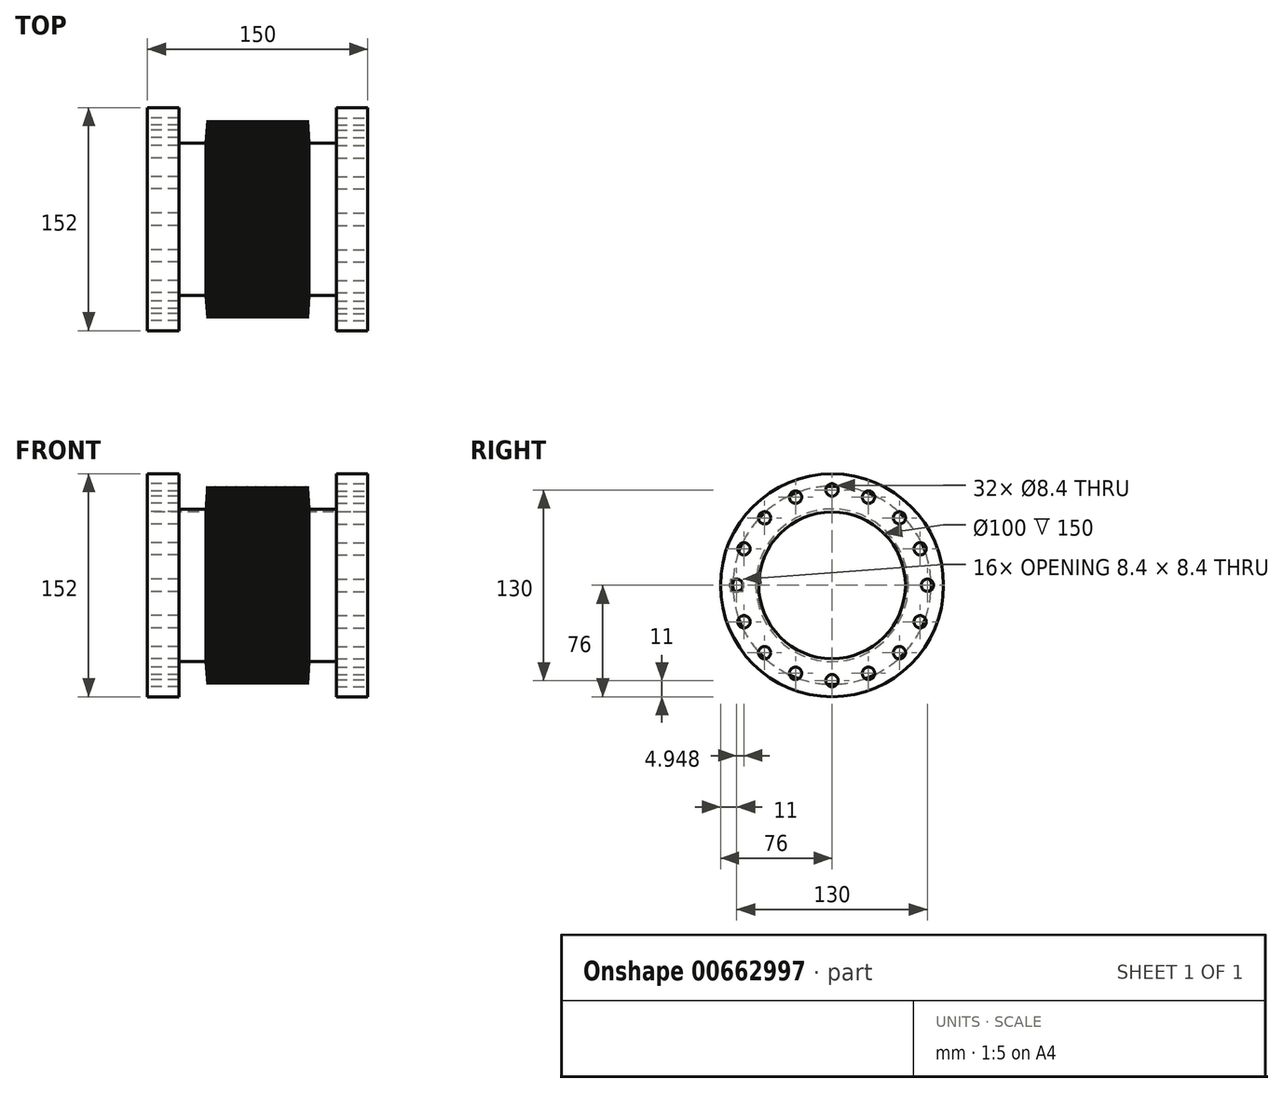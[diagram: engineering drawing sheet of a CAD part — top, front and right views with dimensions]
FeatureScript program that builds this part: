
annotation { "Feature Type Name" : "Feature", "Feature Type Description" : "" }
export const myFeature = defineFeature(function(context is Context, id is Id, definition is map)
    precondition{}
    {
        {
            var Q0;
            Q0=qCreatedBy(makeId("Front.planeOp"),FACE);
            var sketch = newSketch(context, id + "F0", { "sketchPlane" : qUnion([Q0])});
            skLineSegment(sketch, "E0", {"start": v(0, 50) * mm, "end": v(0, 76) * mm});
            skLineSegment(sketch, "E1", {"start": v(0, 76) * mm, "end": v(21.3, 76) * mm});
            skLineSegment(sketch, "E2", {"start": v(21.3, 76) * mm, "end": v(21.3, 52) * mm});
            skLineSegment(sketch, "E3", {"start": v(21.3, 52) * mm, "end": v(40, 52) * mm});
            skLineSegment(sketch, "E4", {"start": v(40, 52) * mm, "end": v(41, 67.5) * mm});
            skLineSegment(sketch, "E5", {"start": v(41, 67.5) * mm, "end": v(42, 52) * mm});
            skLineSegment(sketch, "E6", {"start": v(41, 67.5) * mm, "end": v(41, 52) * mm, "construction": true});
            skLineSegment(sketch, "E7", {"start": v(40, 52) * mm, "end": v(41, 52) * mm, "construction": true});
            skLineSegment(sketch, "E8", {"start": v(41, 52) * mm, "end": v(42, 52) * mm, "construction": true});
            skLineSegment(sketch, "E9.1.0.0", {"start": v(42, 52) * mm, "end": v(43, 67.5) * mm});
            skLineSegment(sketch, "E9.1.0.1", {"start": v(43, 67.5) * mm, "end": v(44, 52) * mm});
            skLineSegment(sketch, "E9.2.0.0", {"start": v(44, 52) * mm, "end": v(45, 67.5) * mm});
            skLineSegment(sketch, "E9.2.0.1", {"start": v(45, 67.5) * mm, "end": v(46, 52) * mm});
            skLineSegment(sketch, "E9.3.0.0", {"start": v(46, 52) * mm, "end": v(47, 67.5) * mm});
            skLineSegment(sketch, "E9.3.0.1", {"start": v(47, 67.5) * mm, "end": v(48, 52) * mm});
            skLineSegment(sketch, "E9.4.0.0", {"start": v(48, 52) * mm, "end": v(49, 67.5) * mm});
            skLineSegment(sketch, "E9.4.0.1", {"start": v(49, 67.5) * mm, "end": v(50, 52) * mm});
            skLineSegment(sketch, "E9.5.0.0", {"start": v(50, 52) * mm, "end": v(51, 67.5) * mm});
            skLineSegment(sketch, "E9.5.0.1", {"start": v(51, 67.5) * mm, "end": v(52, 52) * mm});
            skLineSegment(sketch, "E9.6.0.0", {"start": v(52, 52) * mm, "end": v(53, 67.5) * mm});
            skLineSegment(sketch, "E9.6.0.1", {"start": v(53, 67.5) * mm, "end": v(54, 52) * mm});
            skLineSegment(sketch, "E9.7.0.0", {"start": v(54, 52) * mm, "end": v(55, 67.5) * mm});
            skLineSegment(sketch, "E9.7.0.1", {"start": v(55, 67.5) * mm, "end": v(56, 52) * mm});
            skLineSegment(sketch, "E9.8.0.0", {"start": v(56, 52) * mm, "end": v(57, 67.5) * mm});
            skLineSegment(sketch, "E9.8.0.1", {"start": v(57, 67.5) * mm, "end": v(58, 52) * mm});
            skLineSegment(sketch, "E9.9.0.0", {"start": v(58, 52) * mm, "end": v(59, 67.5) * mm});
            skLineSegment(sketch, "E9.9.0.1", {"start": v(59, 67.5) * mm, "end": v(60, 52) * mm});
            skLineSegment(sketch, "E9.10.0.0", {"start": v(60, 52) * mm, "end": v(61, 67.5) * mm});
            skLineSegment(sketch, "E9.10.0.1", {"start": v(61, 67.5) * mm, "end": v(62, 52) * mm});
            skLineSegment(sketch, "E9.11.0.0", {"start": v(62, 52) * mm, "end": v(63, 67.5) * mm});
            skLineSegment(sketch, "E9.11.0.1", {"start": v(63, 67.5) * mm, "end": v(64, 52) * mm});
            skLineSegment(sketch, "E9.12.0.0", {"start": v(64, 52) * mm, "end": v(65, 67.5) * mm});
            skLineSegment(sketch, "E9.12.0.1", {"start": v(65, 67.5) * mm, "end": v(66, 52) * mm});
            skLineSegment(sketch, "E9.13.0.0", {"start": v(66, 52) * mm, "end": v(67, 67.5) * mm});
            skLineSegment(sketch, "E9.13.0.1", {"start": v(67, 67.5) * mm, "end": v(68, 52) * mm});
            skLineSegment(sketch, "E9.14.0.0", {"start": v(68, 52) * mm, "end": v(69, 67.5) * mm});
            skLineSegment(sketch, "E9.14.0.1", {"start": v(69, 67.5) * mm, "end": v(70, 52) * mm});
            skLineSegment(sketch, "E9.15.0.0", {"start": v(70, 52) * mm, "end": v(71, 67.5) * mm});
            skLineSegment(sketch, "E9.15.0.1", {"start": v(71, 67.5) * mm, "end": v(72, 52) * mm});
            skLineSegment(sketch, "E9.16.0.0", {"start": v(72, 52) * mm, "end": v(73, 67.5) * mm});
            skLineSegment(sketch, "E9.16.0.1", {"start": v(73, 67.5) * mm, "end": v(74, 52) * mm});
            skLineSegment(sketch, "E9.17.0.0", {"start": v(74, 52) * mm, "end": v(75, 67.5) * mm});
            skLineSegment(sketch, "E9.17.0.1", {"start": v(75, 67.5) * mm, "end": v(76, 52) * mm});
            skLineSegment(sketch, "E9.18.0.0", {"start": v(76, 52) * mm, "end": v(77, 67.5) * mm});
            skLineSegment(sketch, "E9.18.0.1", {"start": v(77, 67.5) * mm, "end": v(78, 52) * mm});
            skLineSegment(sketch, "E9.19.0.0", {"start": v(78, 52) * mm, "end": v(79, 67.5) * mm});
            skLineSegment(sketch, "E9.19.0.1", {"start": v(79, 67.5) * mm, "end": v(80, 52) * mm});
            skLineSegment(sketch, "E9.20.0.0", {"start": v(80, 52) * mm, "end": v(81, 67.5) * mm});
            skLineSegment(sketch, "E9.20.0.1", {"start": v(81, 67.5) * mm, "end": v(82, 52) * mm});
            skLineSegment(sketch, "E9.21.0.0", {"start": v(82, 52) * mm, "end": v(83, 67.5) * mm});
            skLineSegment(sketch, "E9.21.0.1", {"start": v(83, 67.5) * mm, "end": v(84, 52) * mm});
            skLineSegment(sketch, "E9.22.0.0", {"start": v(84, 52) * mm, "end": v(85, 67.5) * mm});
            skLineSegment(sketch, "E9.22.0.1", {"start": v(85, 67.5) * mm, "end": v(86, 52) * mm});
            skLineSegment(sketch, "E9.23.0.0", {"start": v(86, 52) * mm, "end": v(87, 67.5) * mm});
            skLineSegment(sketch, "E9.23.0.1", {"start": v(87, 67.5) * mm, "end": v(88, 52) * mm});
            skLineSegment(sketch, "E9.24.0.0", {"start": v(88, 52) * mm, "end": v(89, 67.5) * mm});
            skLineSegment(sketch, "E9.24.0.1", {"start": v(89, 67.5) * mm, "end": v(90, 52) * mm});
            skLineSegment(sketch, "E9.25.0.0", {"start": v(90, 52) * mm, "end": v(91, 67.5) * mm});
            skLineSegment(sketch, "E9.25.0.1", {"start": v(91, 67.5) * mm, "end": v(92, 52) * mm});
            skLineSegment(sketch, "E9.26.0.0", {"start": v(92, 52) * mm, "end": v(93, 67.5) * mm});
            skLineSegment(sketch, "E9.26.0.1", {"start": v(93, 67.5) * mm, "end": v(94, 52) * mm});
            skLineSegment(sketch, "E9.27.0.0", {"start": v(94, 52) * mm, "end": v(95, 67.5) * mm});
            skLineSegment(sketch, "E9.27.0.1", {"start": v(95, 67.5) * mm, "end": v(96, 52) * mm});
            skLineSegment(sketch, "E9.28.0.0", {"start": v(96, 52) * mm, "end": v(97, 67.5) * mm});
            skLineSegment(sketch, "E9.28.0.1", {"start": v(97, 67.5) * mm, "end": v(98, 52) * mm});
            skLineSegment(sketch, "E9.29.0.0", {"start": v(98, 52) * mm, "end": v(99, 67.5) * mm});
            skLineSegment(sketch, "E9.29.0.1", {"start": v(99, 67.5) * mm, "end": v(100, 52) * mm});
            skLineSegment(sketch, "E9.30.0.0", {"start": v(100, 52) * mm, "end": v(101, 67.5) * mm});
            skLineSegment(sketch, "E9.30.0.1", {"start": v(101, 67.5) * mm, "end": v(102, 52) * mm});
            skLineSegment(sketch, "E9.31.0.0", {"start": v(102, 52) * mm, "end": v(103, 67.5) * mm});
            skLineSegment(sketch, "E9.31.0.1", {"start": v(103, 67.5) * mm, "end": v(104, 52) * mm});
            skLineSegment(sketch, "E9.32.0.0", {"start": v(104, 52) * mm, "end": v(105, 67.5) * mm});
            skLineSegment(sketch, "E9.32.0.1", {"start": v(105, 67.5) * mm, "end": v(106, 52) * mm});
            skLineSegment(sketch, "E9.33.0.0", {"start": v(106, 52) * mm, "end": v(107, 67.5) * mm});
            skLineSegment(sketch, "E9.33.0.1", {"start": v(107, 67.5) * mm, "end": v(108, 52) * mm});
            skLineSegment(sketch, "E9.34.0.0", {"start": v(108, 52) * mm, "end": v(109, 67.5) * mm});
            skLineSegment(sketch, "E9.34.0.1", {"start": v(109, 67.5) * mm, "end": v(110, 52) * mm});
            skLineSegment(sketch, "E9.direction1", {"start": v(40, 52) * mm, "end": v(42, 52) * mm, "construction": true});
            skLineSegment(sketch, "E10", {"start": v(110, 52) * mm, "end": v(128.7, 52) * mm});
            skLineSegment(sketch, "E11", {"start": v(128.7, 52) * mm, "end": v(128.7, 76) * mm});
            skLineSegment(sketch, "E12", {"start": v(128.7, 76) * mm, "end": v(150, 76) * mm});
            skLineSegment(sketch, "E13", {"start": v(150, 76) * mm, "end": v(150, 50) * mm});
            skLineSegment(sketch, "E14", {"start": v(150, 50) * mm, "end": v(0, 50) * mm});
            skSolve(sketch);
        }
        {
            var Q0;
            Q0=qCreatedBy(makeId("Front.planeOp"),FACE);
            var sketch = newSketch(context, id + "F1", { "sketchPlane" : qUnion([Q0])});
            skLineSegment(sketch, "E15", {"start": v(0, 0) * mm, "end": v(75.04, 0) * mm});
            skSolve(sketch);
        }
        {
            var Q0;
            Q0=makeQuery(id+"F0.imprint","IMPRINT",FACE,{"disambiguationData":[TD([[makeQuery(id+"F0.imprint","IMPRINT",EDGE,{"derivedFrom":sQuery(id+"F0.wireOp",EDGE,"E0")}),-1.0]])]});
            var Q1;
            Q1=sQuery(id+"F1.wireOp",EDGE,"E15");
            revolve(context, id + "F2", {"surfaceOperationType" : NewSurfaceOperationType.NEW, "entities" : qUnion([Q0]), "axis" : qUnion([Q1]), "revolveType" : RevolveType.FULL});
        }
        {
            var Q0;
            Q0=makeQuery(id+"F2.opRevolve","SWEPT_FACE",FACE,{"disambiguationData":[OSD([sQuery(id+"F0.wireOp",EDGE,"E0")])]});
            var sketch = newSketch(context, id + "F3", { "sketchPlane" : qUnion([Q0])});
            skCircle(sketch, "E16", {"center": v(0, 0) * mm, "radius": 65 * mm, "construction": true});
            skPoint(sketch, "E17", {"position": v(-65, 0) * mm});
            skLineSegment(sketch, "E18", {"start": v(-65, 0) * mm, "end": v(0, 0) * mm, "construction": true});
            skPoint(sketch, "E19.1.0", {"position": v(-60.05, -24.87) * mm});
            skPoint(sketch, "E19.2.0", {"position": v(-45.96, -45.96) * mm});
            skPoint(sketch, "E19.3.0", {"position": v(-24.87, -60.05) * mm});
            skPoint(sketch, "E19.4.0", {"position": v(0, -65) * mm});
            skPoint(sketch, "E19.5.0", {"position": v(24.87, -60.05) * mm});
            skPoint(sketch, "E19.6.0", {"position": v(45.96, -45.96) * mm});
            skPoint(sketch, "E19.7.0", {"position": v(60.05, -24.87) * mm});
            skPoint(sketch, "E20.0.8.0", {"position": v(65, 0) * mm});
            skPoint(sketch, "E20.0.9.0", {"position": v(60.05, 24.87) * mm});
            skPoint(sketch, "E20.0.10.0", {"position": v(45.96, 45.96) * mm});
            skPoint(sketch, "E20.0.11.0", {"position": v(24.87, 60.05) * mm});
            skPoint(sketch, "E20.0.12.0", {"position": v(0, 65) * mm});
            skPoint(sketch, "E20.0.13.0", {"position": v(-24.87, 60.05) * mm});
            skPoint(sketch, "E20.0.14.0", {"position": v(-45.96, 45.96) * mm});
            skPoint(sketch, "E20.0.15.0", {"position": v(-60.05, 24.87) * mm});
            skSolve(sketch);
        }
        {
            var Q0;
            Q0=sQuery(id+"F3.wireOp",VERTEX,"E17");
            var Q1;
            Q1=sQuery(id+"F3.wireOp",VERTEX,"E19.7.0");
            var Q2;
            Q2=sQuery(id+"F3.wireOp",VERTEX,"E19.6.0");
            var Q3;
            Q3=sQuery(id+"F3.wireOp",VERTEX,"E19.5.0");
            var Q4;
            Q4=sQuery(id+"F3.wireOp",VERTEX,"E19.4.0");
            var Q5;
            Q5=sQuery(id+"F3.wireOp",VERTEX,"E19.3.0");
            var Q6;
            Q6=sQuery(id+"F3.wireOp",VERTEX,"E19.2.0");
            var Q7;
            Q7=sQuery(id+"F3.wireOp",VERTEX,"E19.1.0");
            var Q8;
            Q8=sQuery(id+"F3.wireOp",VERTEX,"E20.0.15.0");
            var Q9;
            Q9=sQuery(id+"F3.wireOp",VERTEX,"E20.0.14.0");
            var Q10;
            Q10=sQuery(id+"F3.wireOp",VERTEX,"E20.0.13.0");
            var Q11;
            Q11=sQuery(id+"F3.wireOp",VERTEX,"E20.0.12.0");
            var Q12;
            Q12=sQuery(id+"F3.wireOp",VERTEX,"E20.0.11.0");
            var Q13;
            Q13=sQuery(id+"F3.wireOp",VERTEX,"E20.0.10.0");
            var Q14;
            Q14=sQuery(id+"F3.wireOp",VERTEX,"E20.0.9.0");
            var Q15;
            Q15=sQuery(id+"F3.wireOp",VERTEX,"E20.0.8.0");
            var Q16;
            Q16=makeQuery(id+"F2.opRevolve","SWEPT_BODY",BODY,{"disambiguationData":[OSD([sQuery(id+"F0.wireOp",EDGE,"E0"),sQuery(id+"F0.wireOp",EDGE,"E1"),sQuery(id+"F0.wireOp",EDGE,"E2"),sQuery(id+"F0.wireOp",EDGE,"E3"),sQuery(id+"F0.wireOp",EDGE,"E4"),sQuery(id+"F0.wireOp",EDGE,"E5"),sQuery(id+"F0.wireOp",EDGE,"E9.1.0.0"),sQuery(id+"F0.wireOp",EDGE,"E9.1.0.1"),sQuery(id+"F0.wireOp",EDGE,"E9.2.0.0"),sQuery(id+"F0.wireOp",EDGE,"E9.2.0.1"),sQuery(id+"F0.wireOp",EDGE,"E9.3.0.0"),sQuery(id+"F0.wireOp",EDGE,"E9.3.0.1"),sQuery(id+"F0.wireOp",EDGE,"E9.4.0.0"),sQuery(id+"F0.wireOp",EDGE,"E9.4.0.1"),sQuery(id+"F0.wireOp",EDGE,"E9.5.0.0"),sQuery(id+"F0.wireOp",EDGE,"E9.5.0.1"),sQuery(id+"F0.wireOp",EDGE,"E9.6.0.0"),sQuery(id+"F0.wireOp",EDGE,"E9.6.0.1"),sQuery(id+"F0.wireOp",EDGE,"E9.7.0.0"),sQuery(id+"F0.wireOp",EDGE,"E9.7.0.1"),sQuery(id+"F0.wireOp",EDGE,"E9.8.0.0"),sQuery(id+"F0.wireOp",EDGE,"E9.8.0.1"),sQuery(id+"F0.wireOp",EDGE,"E9.9.0.0"),sQuery(id+"F0.wireOp",EDGE,"E9.9.0.1"),sQuery(id+"F0.wireOp",EDGE,"E9.10.0.0"),sQuery(id+"F0.wireOp",EDGE,"E9.10.0.1"),sQuery(id+"F0.wireOp",EDGE,"E9.11.0.0"),sQuery(id+"F0.wireOp",EDGE,"E9.11.0.1"),sQuery(id+"F0.wireOp",EDGE,"E9.12.0.0"),sQuery(id+"F0.wireOp",EDGE,"E9.12.0.1"),sQuery(id+"F0.wireOp",EDGE,"E9.13.0.0"),sQuery(id+"F0.wireOp",EDGE,"E9.13.0.1"),sQuery(id+"F0.wireOp",EDGE,"E9.14.0.0"),sQuery(id+"F0.wireOp",EDGE,"E9.14.0.1"),sQuery(id+"F0.wireOp",EDGE,"E9.15.0.0"),sQuery(id+"F0.wireOp",EDGE,"E9.15.0.1"),sQuery(id+"F0.wireOp",EDGE,"E9.16.0.0"),sQuery(id+"F0.wireOp",EDGE,"E9.16.0.1"),sQuery(id+"F0.wireOp",EDGE,"E9.17.0.0"),sQuery(id+"F0.wireOp",EDGE,"E9.17.0.1"),sQuery(id+"F0.wireOp",EDGE,"E9.18.0.0"),sQuery(id+"F0.wireOp",EDGE,"E9.18.0.1"),sQuery(id+"F0.wireOp",EDGE,"E9.19.0.0"),sQuery(id+"F0.wireOp",EDGE,"E9.19.0.1"),sQuery(id+"F0.wireOp",EDGE,"E9.20.0.0"),sQuery(id+"F0.wireOp",EDGE,"E9.20.0.1"),sQuery(id+"F0.wireOp",EDGE,"E9.21.0.0"),sQuery(id+"F0.wireOp",EDGE,"E9.21.0.1"),sQuery(id+"F0.wireOp",EDGE,"E9.22.0.0"),sQuery(id+"F0.wireOp",EDGE,"E9.22.0.1"),sQuery(id+"F0.wireOp",EDGE,"E9.23.0.0"),sQuery(id+"F0.wireOp",EDGE,"E9.23.0.1"),sQuery(id+"F0.wireOp",EDGE,"E9.24.0.0"),sQuery(id+"F0.wireOp",EDGE,"E9.24.0.1"),sQuery(id+"F0.wireOp",EDGE,"E9.25.0.0"),sQuery(id+"F0.wireOp",EDGE,"E9.25.0.1"),sQuery(id+"F0.wireOp",EDGE,"E9.26.0.0"),sQuery(id+"F0.wireOp",EDGE,"E9.26.0.1"),sQuery(id+"F0.wireOp",EDGE,"E9.27.0.0"),sQuery(id+"F0.wireOp",EDGE,"E9.27.0.1"),sQuery(id+"F0.wireOp",EDGE,"E9.28.0.0"),sQuery(id+"F0.wireOp",EDGE,"E9.28.0.1"),sQuery(id+"F0.wireOp",EDGE,"E9.29.0.0"),sQuery(id+"F0.wireOp",EDGE,"E9.29.0.1"),sQuery(id+"F0.wireOp",EDGE,"E9.30.0.0"),sQuery(id+"F0.wireOp",EDGE,"E9.30.0.1"),sQuery(id+"F0.wireOp",EDGE,"E9.31.0.0"),sQuery(id+"F0.wireOp",EDGE,"E9.31.0.1"),sQuery(id+"F0.wireOp",EDGE,"E9.32.0.0"),sQuery(id+"F0.wireOp",EDGE,"E9.32.0.1"),sQuery(id+"F0.wireOp",EDGE,"E9.33.0.0"),sQuery(id+"F0.wireOp",EDGE,"E9.33.0.1"),sQuery(id+"F0.wireOp",EDGE,"E9.34.0.0"),sQuery(id+"F0.wireOp",EDGE,"E9.34.0.1"),sQuery(id+"F0.wireOp",EDGE,"E10"),sQuery(id+"F0.wireOp",EDGE,"E11"),sQuery(id+"F0.wireOp",EDGE,"E12"),sQuery(id+"F0.wireOp",EDGE,"E13"),sQuery(id+"F0.wireOp",EDGE,"E14")])]});
            hole(context, id + "F4", {"style" : HoleStyle.SIMPLE, "endStyle" : HoleEndStyle.BLIND, "standardTappedOrClearance" : lookupTablePath({ "fit" : "Close", "standard" : "ISO", "size" : "M8", "type" : "Clearance" }), "standardBlindInLast" : lookupTablePath({ "fit" : "Close", "standard" : "ISO", "engagement" : "75%", "pitch" : "1.25 mm", "size" : "M8", "type" : "Clearance & tapped" }), "holeDiameter" : 8.4 * mm, "majorDiameter" : 5 * mm, "holeDepth" : 24 * mm, "isTappedThrough" : true, "tappedDepth" : 12 * mm, "tapClearance" : 3, "locations" : qUnion([Q0, Q1, Q2, Q3, Q4, Q5, Q6, Q7, Q8, Q9, Q10, Q11, Q12, Q13, Q14, Q15]), "scope" : qUnion([Q16])});
        }
        {
            var Q0;
            Q0=makeQuery(id+"F2.opRevolve","SWEPT_FACE",FACE,{"disambiguationData":[OSD([sQuery(id+"F0.wireOp",EDGE,"E13")])]});
            var sketch = newSketch(context, id + "F5", { "sketchPlane" : qUnion([Q0])});
            skCircle(sketch, "E21", {"center": v(0, 0) * mm, "radius": 65 * mm, "construction": true});
            skPoint(sketch, "E22", {"position": v(65, 0) * mm});
            skLineSegment(sketch, "E23", {"start": v(65, 0) * mm, "end": v(0, 0) * mm, "construction": true});
            skPoint(sketch, "E24.1.0", {"position": v(60.05, 24.87) * mm});
            skPoint(sketch, "E24.2.0", {"position": v(45.96, 45.96) * mm});
            skPoint(sketch, "E24.3.0", {"position": v(24.87, 60.05) * mm});
            skPoint(sketch, "E24.4.0", {"position": v(0, 65) * mm});
            skPoint(sketch, "E24.5.0", {"position": v(-24.87, 60.05) * mm});
            skPoint(sketch, "E24.6.0", {"position": v(-45.96, 45.96) * mm});
            skPoint(sketch, "E24.7.0", {"position": v(-60.05, 24.87) * mm});
            skPoint(sketch, "E25.0.8.0", {"position": v(-65, 0) * mm});
            skPoint(sketch, "E25.0.9.0", {"position": v(-60.05, -24.87) * mm});
            skPoint(sketch, "E25.0.10.0", {"position": v(-45.96, -45.96) * mm});
            skPoint(sketch, "E25.0.11.0", {"position": v(-24.87, -60.05) * mm});
            skPoint(sketch, "E25.0.12.0", {"position": v(0, -65) * mm});
            skPoint(sketch, "E25.0.13.0", {"position": v(24.87, -60.05) * mm});
            skPoint(sketch, "E25.0.14.0", {"position": v(45.96, -45.96) * mm});
            skPoint(sketch, "E25.0.15.0", {"position": v(60.05, -24.87) * mm});
            skSolve(sketch);
        }
        {
            var Q0;
            Q0=sQuery(id+"F5.wireOp",VERTEX,"E22");
            var Q1;
            Q1=sQuery(id+"F5.wireOp",VERTEX,"E24.7.0");
            var Q2;
            Q2=sQuery(id+"F5.wireOp",VERTEX,"E24.6.0");
            var Q3;
            Q3=sQuery(id+"F5.wireOp",VERTEX,"E24.5.0");
            var Q4;
            Q4=sQuery(id+"F5.wireOp",VERTEX,"E24.4.0");
            var Q5;
            Q5=sQuery(id+"F5.wireOp",VERTEX,"E24.3.0");
            var Q6;
            Q6=sQuery(id+"F5.wireOp",VERTEX,"E24.2.0");
            var Q7;
            Q7=sQuery(id+"F5.wireOp",VERTEX,"E24.1.0");
            var Q8;
            Q8=sQuery(id+"F5.wireOp",VERTEX,"E25.0.15.0");
            var Q9;
            Q9=sQuery(id+"F5.wireOp",VERTEX,"E25.0.14.0");
            var Q10;
            Q10=sQuery(id+"F5.wireOp",VERTEX,"E25.0.13.0");
            var Q11;
            Q11=sQuery(id+"F5.wireOp",VERTEX,"E25.0.12.0");
            var Q12;
            Q12=sQuery(id+"F5.wireOp",VERTEX,"E25.0.11.0");
            var Q13;
            Q13=sQuery(id+"F5.wireOp",VERTEX,"E25.0.10.0");
            var Q14;
            Q14=sQuery(id+"F5.wireOp",VERTEX,"E25.0.9.0");
            var Q15;
            Q15=sQuery(id+"F5.wireOp",VERTEX,"E25.0.8.0");
            var Q16;
            Q16=makeQuery(id+"F2.opRevolve","SWEPT_BODY",BODY,{"disambiguationData":[OSD([sQuery(id+"F0.wireOp",EDGE,"E0"),sQuery(id+"F0.wireOp",EDGE,"E1"),sQuery(id+"F0.wireOp",EDGE,"E2"),sQuery(id+"F0.wireOp",EDGE,"E3"),sQuery(id+"F0.wireOp",EDGE,"E4"),sQuery(id+"F0.wireOp",EDGE,"E5"),sQuery(id+"F0.wireOp",EDGE,"E9.1.0.0"),sQuery(id+"F0.wireOp",EDGE,"E9.1.0.1"),sQuery(id+"F0.wireOp",EDGE,"E9.2.0.0"),sQuery(id+"F0.wireOp",EDGE,"E9.2.0.1"),sQuery(id+"F0.wireOp",EDGE,"E9.3.0.0"),sQuery(id+"F0.wireOp",EDGE,"E9.3.0.1"),sQuery(id+"F0.wireOp",EDGE,"E9.4.0.0"),sQuery(id+"F0.wireOp",EDGE,"E9.4.0.1"),sQuery(id+"F0.wireOp",EDGE,"E9.5.0.0"),sQuery(id+"F0.wireOp",EDGE,"E9.5.0.1"),sQuery(id+"F0.wireOp",EDGE,"E9.6.0.0"),sQuery(id+"F0.wireOp",EDGE,"E9.6.0.1"),sQuery(id+"F0.wireOp",EDGE,"E9.7.0.0"),sQuery(id+"F0.wireOp",EDGE,"E9.7.0.1"),sQuery(id+"F0.wireOp",EDGE,"E9.8.0.0"),sQuery(id+"F0.wireOp",EDGE,"E9.8.0.1"),sQuery(id+"F0.wireOp",EDGE,"E9.9.0.0"),sQuery(id+"F0.wireOp",EDGE,"E9.9.0.1"),sQuery(id+"F0.wireOp",EDGE,"E9.10.0.0"),sQuery(id+"F0.wireOp",EDGE,"E9.10.0.1"),sQuery(id+"F0.wireOp",EDGE,"E9.11.0.0"),sQuery(id+"F0.wireOp",EDGE,"E9.11.0.1"),sQuery(id+"F0.wireOp",EDGE,"E9.12.0.0"),sQuery(id+"F0.wireOp",EDGE,"E9.12.0.1"),sQuery(id+"F0.wireOp",EDGE,"E9.13.0.0"),sQuery(id+"F0.wireOp",EDGE,"E9.13.0.1"),sQuery(id+"F0.wireOp",EDGE,"E9.14.0.0"),sQuery(id+"F0.wireOp",EDGE,"E9.14.0.1"),sQuery(id+"F0.wireOp",EDGE,"E9.15.0.0"),sQuery(id+"F0.wireOp",EDGE,"E9.15.0.1"),sQuery(id+"F0.wireOp",EDGE,"E9.16.0.0"),sQuery(id+"F0.wireOp",EDGE,"E9.16.0.1"),sQuery(id+"F0.wireOp",EDGE,"E9.17.0.0"),sQuery(id+"F0.wireOp",EDGE,"E9.17.0.1"),sQuery(id+"F0.wireOp",EDGE,"E9.18.0.0"),sQuery(id+"F0.wireOp",EDGE,"E9.18.0.1"),sQuery(id+"F0.wireOp",EDGE,"E9.19.0.0"),sQuery(id+"F0.wireOp",EDGE,"E9.19.0.1"),sQuery(id+"F0.wireOp",EDGE,"E9.20.0.0"),sQuery(id+"F0.wireOp",EDGE,"E9.20.0.1"),sQuery(id+"F0.wireOp",EDGE,"E9.21.0.0"),sQuery(id+"F0.wireOp",EDGE,"E9.21.0.1"),sQuery(id+"F0.wireOp",EDGE,"E9.22.0.0"),sQuery(id+"F0.wireOp",EDGE,"E9.22.0.1"),sQuery(id+"F0.wireOp",EDGE,"E9.23.0.0"),sQuery(id+"F0.wireOp",EDGE,"E9.23.0.1"),sQuery(id+"F0.wireOp",EDGE,"E9.24.0.0"),sQuery(id+"F0.wireOp",EDGE,"E9.24.0.1"),sQuery(id+"F0.wireOp",EDGE,"E9.25.0.0"),sQuery(id+"F0.wireOp",EDGE,"E9.25.0.1"),sQuery(id+"F0.wireOp",EDGE,"E9.26.0.0"),sQuery(id+"F0.wireOp",EDGE,"E9.26.0.1"),sQuery(id+"F0.wireOp",EDGE,"E9.27.0.0"),sQuery(id+"F0.wireOp",EDGE,"E9.27.0.1"),sQuery(id+"F0.wireOp",EDGE,"E9.28.0.0"),sQuery(id+"F0.wireOp",EDGE,"E9.28.0.1"),sQuery(id+"F0.wireOp",EDGE,"E9.29.0.0"),sQuery(id+"F0.wireOp",EDGE,"E9.29.0.1"),sQuery(id+"F0.wireOp",EDGE,"E9.30.0.0"),sQuery(id+"F0.wireOp",EDGE,"E9.30.0.1"),sQuery(id+"F0.wireOp",EDGE,"E9.31.0.0"),sQuery(id+"F0.wireOp",EDGE,"E9.31.0.1"),sQuery(id+"F0.wireOp",EDGE,"E9.32.0.0"),sQuery(id+"F0.wireOp",EDGE,"E9.32.0.1"),sQuery(id+"F0.wireOp",EDGE,"E9.33.0.0"),sQuery(id+"F0.wireOp",EDGE,"E9.33.0.1"),sQuery(id+"F0.wireOp",EDGE,"E9.34.0.0"),sQuery(id+"F0.wireOp",EDGE,"E9.34.0.1"),sQuery(id+"F0.wireOp",EDGE,"E10"),sQuery(id+"F0.wireOp",EDGE,"E11"),sQuery(id+"F0.wireOp",EDGE,"E12"),sQuery(id+"F0.wireOp",EDGE,"E13"),sQuery(id+"F0.wireOp",EDGE,"E14")])]});
            hole(context, id + "F6", {"style" : HoleStyle.SIMPLE, "endStyle" : HoleEndStyle.BLIND, "standardTappedOrClearance" : lookupTablePath({ "fit" : "Close", "standard" : "ISO", "size" : "M8", "type" : "Clearance" }), "standardBlindInLast" : lookupTablePath({ "fit" : "Close", "standard" : "ISO", "engagement" : "75%", "pitch" : "1.25 mm", "size" : "M8", "type" : "Clearance & tapped" }), "holeDiameter" : 8.4 * mm, "majorDiameter" : 5 * mm, "holeDepth" : 24 * mm, "isTappedThrough" : true, "tappedDepth" : 12 * mm, "tapClearance" : 3, "locations" : qUnion([Q0, Q1, Q2, Q3, Q4, Q5, Q6, Q7, Q8, Q9, Q10, Q11, Q12, Q13, Q14, Q15]), "scope" : qUnion([Q16])});
        }
    });
